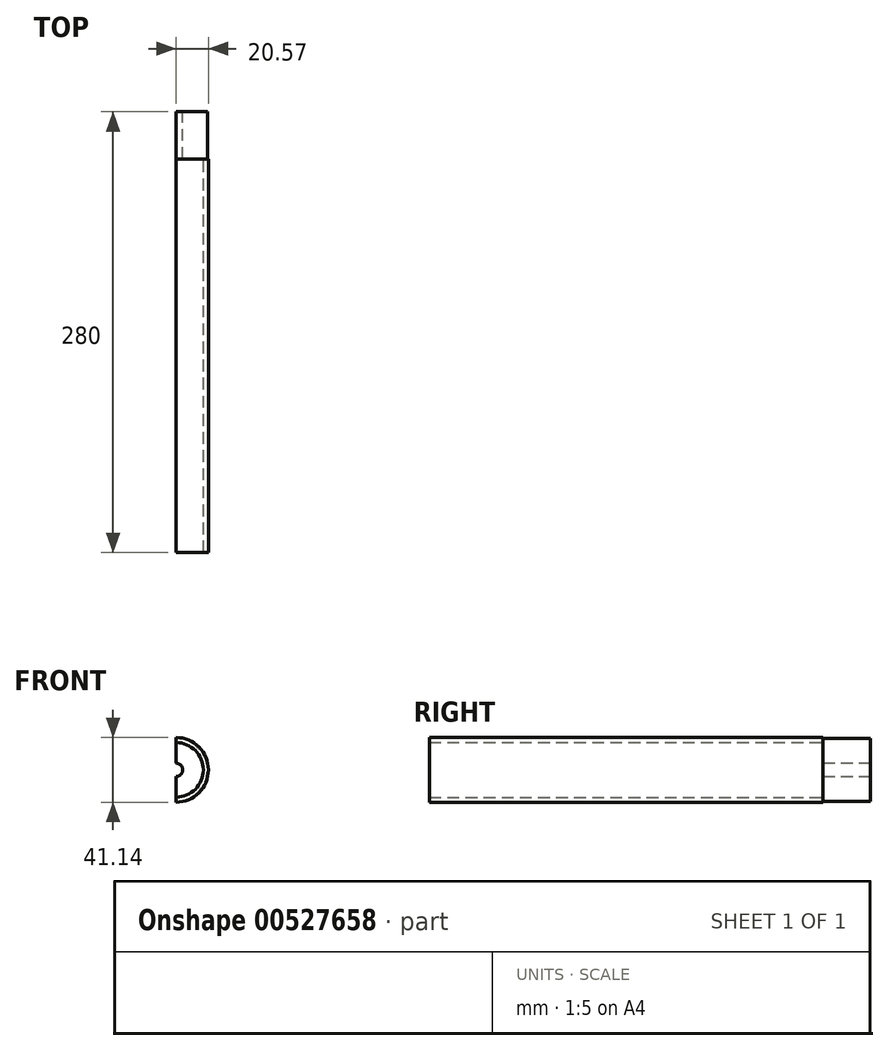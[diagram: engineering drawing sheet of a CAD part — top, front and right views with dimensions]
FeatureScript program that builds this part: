
annotation { "Feature Type Name" : "Feature", "Feature Type Description" : "" }
export const myFeature = defineFeature(function(context is Context, id is Id, definition is map)
    precondition{}
    {
        {
            var Q0;
            Q0=qCreatedBy(makeId("Front.planeOp"),FACE);
            var sketch = newSketch(context, id + "F0", { "sketchPlane" : qUnion([Q0])});
            skCircle(sketch, "E0", {"center": v(0, 0) * mm, "radius": 17.33 * mm});
            skCircle(sketch, "E1", {"center": v(0, 0) * mm, "radius": 20.57 * mm});
            skSolve(sketch);
        }
        {
            var Q0;
            Q0=makeQuery(id+"F0.imprint","IMPRINT",FACE,{"disambiguationData":[TD([[makeQuery(id+"F0.imprint","IMPRINT",EDGE,{"derivedFrom":sQuery(id+"F0.wireOp",EDGE,"E0")}),-1.0]])]});
            extrude(context, id + "F1", {"entities" : qUnion([Q0]), "depth" : 250 * mm, "offsetDistance" : 25 * mm});
        }
        {
            var Q0;
            Q0=qCreatedBy(makeId("Front.planeOp"),FACE);
            var sketch = newSketch(context, id + "F2", { "sketchPlane" : qUnion([Q0])});
            skCircle(sketch, "E2", {"center": v(0, 0) * mm, "radius": 19.94 * mm});
            skSolve(sketch);
        }
        {
            var Q0;
            Q0=makeQuery(id+"F2.imprint","IMPRINT",FACE,{"disambiguationData":[TD([[makeQuery(id+"F2.imprint","IMPRINT",EDGE,{"derivedFrom":sQuery(id+"F2.wireOp",EDGE,"E2")}),1.0]])]});
            extrude(context, id + "F3", {"entities" : qUnion([Q0]), "operationType" : NewBodyOperationType.ADD, "oppositeDirection" : true, "depth" : 5 * mm, "offsetDistance" : 25 * mm});
        }
        {
            var Q0;
            Q0=makeQuery(id+"F3.opExtrude","CAP_FACE",FACE,{"disambiguationData":[OSD([sQuery(id+"F2.wireOp",EDGE,"E2")])],"isStart":false});
            var sketch = newSketch(context, id + "F4", { "sketchPlane" : qUnion([Q0])});
            skCircle(sketch, "E3", {"center": v(0, 0) * mm, "radius": 3.85 * mm});
            skSolve(sketch);
        }
        {
            var Q0;
            Q0=makeQuery(id+"F4.imprint","IMPRINT",FACE,{"disambiguationData":[TD([[makeQuery(id+"F4.imprint","IMPRINT",EDGE,{"derivedFrom":sQuery(id+"F4.wireOp",EDGE,"E3")}),-1.0]])]});
            var Q1;
            Q1=makeQuery(id+"F4.imprint","IMPRINT",FACE,{"disambiguationData":[TD([[makeQuery(id+"F4.imprint","IMPRINT",EDGE,{"derivedFrom":sQuery(id+"F4.wireOp",EDGE,"E3")}),1.0]])]});
            var Q2;
            Q2=makeQuery(id+"F3.opExtrude","CAP_FACE",FACE,{"disambiguationData":[OSD([sQuery(id+"F2.wireOp",EDGE,"E2")])],"isStart":false});
            var Q3;
            Q3=makeQuery(id+"F3.opExtrude","CAP_FACE",FACE,{"disambiguationData":[OSD([sQuery(id+"F2.wireOp",EDGE,"E2")])],"isStart":true});
            extrude(context, id + "F5", {"entities" : qUnion([Q0, Q1, Q2, Q3]), "operationType" : NewBodyOperationType.ADD, "depth" : 25 * mm, "offsetDistance" : 25 * mm});
        }
        {
            var Q0;
            {var subQ0=sQuery(id+"F2.wireOp",EDGE,"E2");Q0=makeQuery(id+"F5.opExtrude","CAP_FACE",FACE,{"disambiguationData":[OSD([subQ0]),TDD([makeQuery(id+"F3.opExtrude","CAP_FACE",FACE,{"disambiguationData":[OSD([subQ0])],"isStart":false})])],"isStart":false});}
            var sketch = newSketch(context, id + "F6", { "sketchPlane" : qUnion([Q0])});
            skCircle(sketch, "E4", {"center": v(0, 0) * mm, "radius": 4.28 * mm});
            skSolve(sketch);
        }
        {
            var Q0;
            Q0=makeQuery(id+"F6.imprint","IMPRINT",FACE,{"disambiguationData":[TD([[makeQuery(id+"F6.imprint","IMPRINT",EDGE,{"derivedFrom":sQuery(id+"F6.wireOp",EDGE,"E4")}),1.0]])]});
            extrude(context, id + "F7", {"entities" : qUnion([Q0]), "operationType" : NewBodyOperationType.REMOVE, "oppositeDirection" : true, "depth" : 153 * mm, "offsetDistance" : 25 * mm});
        }
        {
            var Q0;
            Q0=qCreatedBy(makeId("Right.planeOp"),FACE);
            var sketch = newSketch(context, id + "F8", { "sketchPlane" : qUnion([Q0])});
            skLineSegment(sketch, "E5.bottom", {"start": v(89.76, 155.8) * mm, "end": v(-365.03, 155.8) * mm});
            skLineSegment(sketch, "E5.top", {"start": v(89.76, -104.55) * mm, "end": v(-365.03, -104.55) * mm});
            skLineSegment(sketch, "E5.left", {"start": v(89.76, 155.8) * mm, "end": v(89.76, -104.55) * mm});
            skLineSegment(sketch, "E5.right", {"start": v(-365.03, 155.8) * mm, "end": v(-365.03, -104.55) * mm});
            skSolve(sketch);
        }
        {
            var Q0;
            Q0=makeQuery(id+"F8.imprint","IMPRINT",FACE,{"disambiguationData":[TD([[makeQuery(id+"F8.imprint","IMPRINT",EDGE,{"derivedFrom":sQuery(id+"F8.wireOp",EDGE,"E5.bottom")}),1.0]])]});
            extrude(context, id + "F9", {"entities" : qUnion([Q0]), "operationType" : NewBodyOperationType.REMOVE, "oppositeDirection" : true, "depth" : 142 * mm, "offsetDistance" : 25 * mm});
        }
    });
